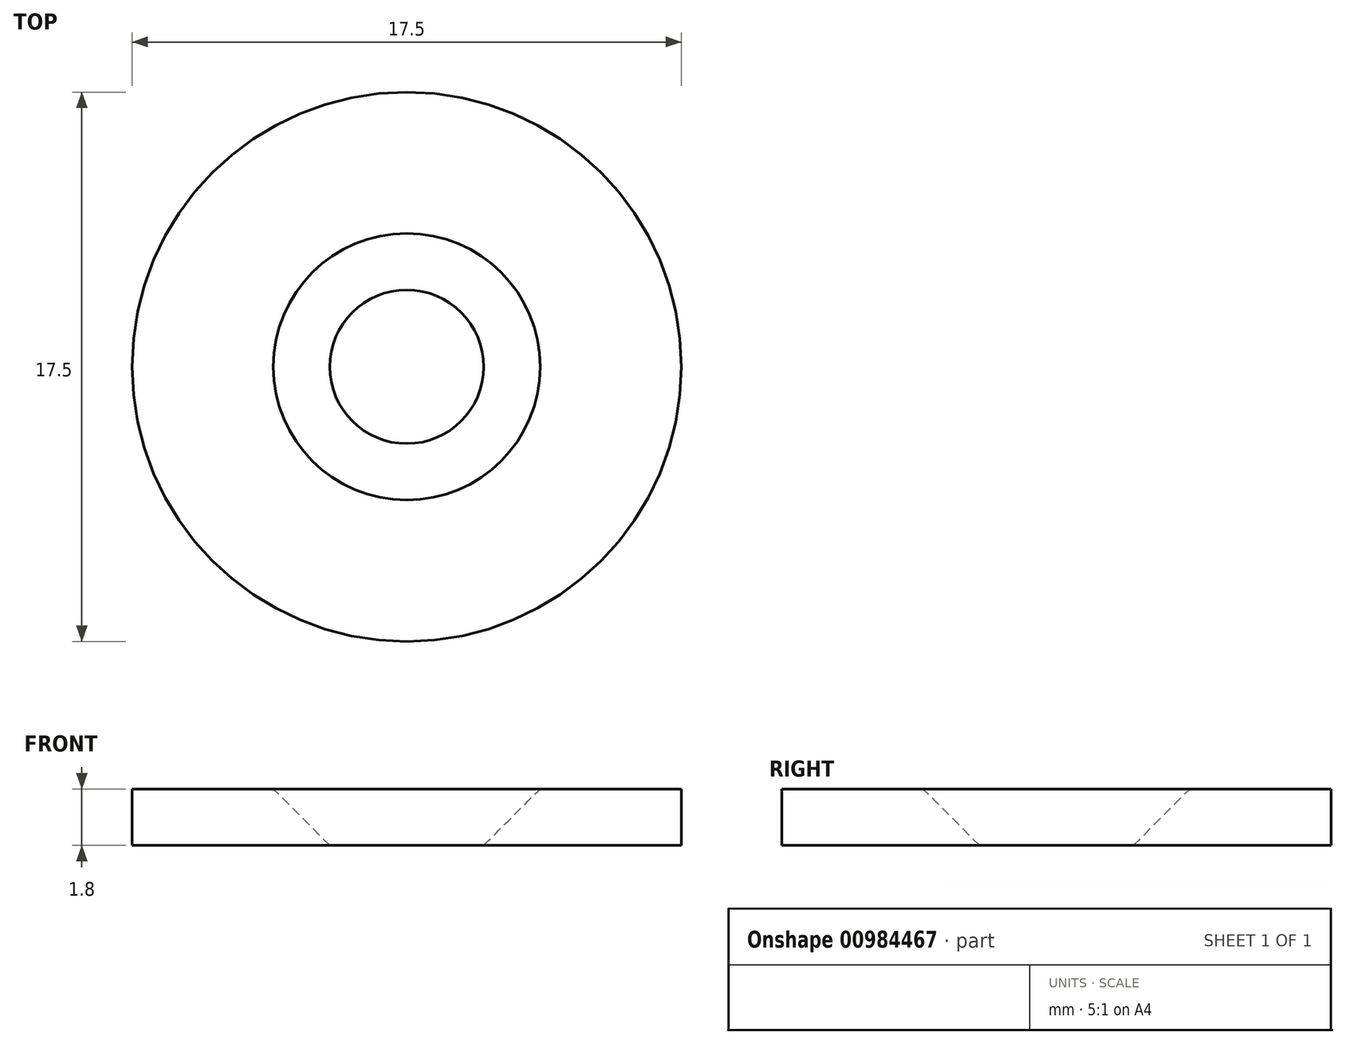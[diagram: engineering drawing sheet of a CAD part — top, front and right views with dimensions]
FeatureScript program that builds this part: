
annotation { "Feature Type Name" : "Feature", "Feature Type Description" : "" }
export const myFeature = defineFeature(function(context is Context, id is Id, definition is map)
    precondition{}
    {
        {
            var Q0;
            Q0=qCreatedBy(makeId("Top.planeOp"),FACE);
            var sketch = newSketch(context, id + "F0", { "sketchPlane" : qUnion([Q0])});
            skCircle(sketch, "E0", {"center": v(0, 0) * mm, "radius": 8.75 * mm});
            skSolve(sketch);
        }
        {
            var Q0;
            Q0=makeQuery(id+"F0.imprint","IMPRINT",FACE,{"disambiguationData":[TD([[makeQuery(id+"F0.imprint","IMPRINT",EDGE,{"derivedFrom":sQuery(id+"F0.wireOp",EDGE,"E0")}),1.0]])]});
            extrude(context, id + "F1", {"entities" : qUnion([Q0]), "depth" : 1.8 * mm, "offsetDistance" : 25 * mm});
        }
        {
            var Q0;
            Q0=makeQuery(id+"F1.opExtrude","CAP_FACE",FACE,{"disambiguationData":[OSD([sQuery(id+"F0.wireOp",EDGE,"E0")])],"isStart":false});
            var sketch = newSketch(context, id + "F2", { "sketchPlane" : qUnion([Q0])});
            skCircle(sketch, "E1", {"center": v(0, 0) * mm, "radius": 4.25 * mm});
            skSolve(sketch);
        }
        {
            var Q0;
            Q0=sQuery(id+"F2.wireOp",VERTEX,"E1.center");
            var Q1;
            Q1=makeQuery(id+"F1.opExtrude","SWEPT_BODY",BODY,{"disambiguationData":[OSD([sQuery(id+"F0.wireOp",EDGE,"E0")])]});
            hole(context, id + "F3", {"style" : HoleStyle.C_SINK, "endStyle" : HoleEndStyle.BLIND, "holeDiameter" : 4 * mm, "cSinkDiameter" : 8.5 * mm, "cSinkAngle" : 90 * degree, "majorDiameter" : 5 * mm, "holeDepth" : 10 * mm, "isTappedThrough" : true, "tappedDepth" : 12 * mm, "tapClearance" : 3, "locations" : qUnion([Q0]), "scope" : qUnion([Q1])});
        }
    });
